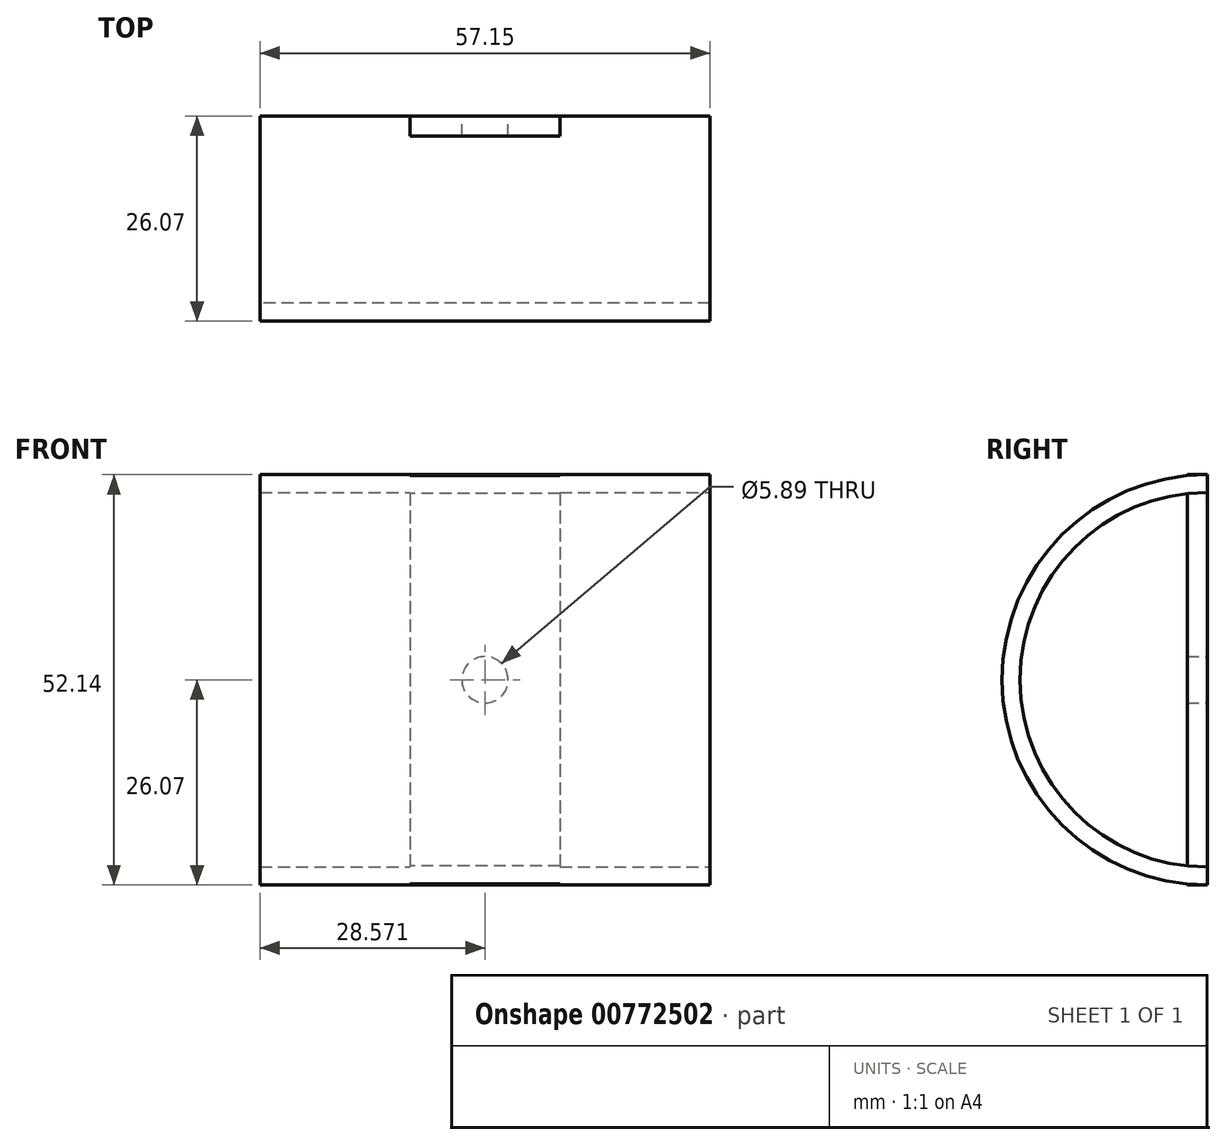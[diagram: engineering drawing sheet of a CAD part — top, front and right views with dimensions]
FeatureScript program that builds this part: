
annotation { "Feature Type Name" : "Feature", "Feature Type Description" : "" }
export const myFeature = defineFeature(function(context is Context, id is Id, definition is map)
    precondition{}
    {
        {
            var Q0;
            Q0=qCreatedBy(makeId("Front.planeOp"),FACE);
            var sketch = newSketch(context, id + "F0", { "sketchPlane" : qUnion([Q0])});
            skLineSegment(sketch, "E0.bottom", {"start": v(-15.82, 23.8) * mm, "end": v(41.33, 23.8) * mm});
            skLineSegment(sketch, "E0.top", {"start": v(-15.82, 26.07) * mm, "end": v(41.33, 26.07) * mm});
            skLineSegment(sketch, "E0.left", {"start": v(-15.82, 23.8) * mm, "end": v(-15.82, 26.07) * mm});
            skLineSegment(sketch, "E0.right", {"start": v(41.33, 23.8) * mm, "end": v(41.33, 26.07) * mm});
            skLineSegment(sketch, "E1", {"start": v(-10.59, 0) * mm, "end": v(36.32, 0) * mm});
            skSolve(sketch);
        }
        {
            var Q0;
            Q0=makeQuery(id+"F0.imprint","IMPRINT",FACE,{"disambiguationData":[TD([[makeQuery(id+"F0.imprint","IMPRINT",EDGE,{"derivedFrom":sQuery(id+"F0.wireOp",EDGE,"E0.bottom")}),1.0]])]});
            var Q1;
            Q1=sQuery(id+"F0.wireOp",EDGE,"E1");
            revolve(context, id + "F1", {"surfaceOperationType" : NewSurfaceOperationType.NEW, "entities" : qUnion([Q0]), "axis" : qUnion([Q1]), "revolveType" : RevolveType.ONE_DIRECTION, "angle" : 180 * degree});
        }
        {
            var Q0;
            Q0=qCreatedBy(makeId("Front.planeOp"),FACE);
            var sketch = newSketch(context, id + "F2", { "sketchPlane" : qUnion([Q0])});
            skCircle(sketch, "E2", {"center": v(12.75, 0) * mm, "radius": 2.94 * mm});
            skLineSegment(sketch, "E3.0", {"start": v(-15.82, 26.07) * mm, "end": v(41.33, 26.07) * mm});
            skLineSegment(sketch, "E4.0", {"start": v(-15.82, -26.07) * mm, "end": v(41.33, -26.07) * mm});
            skLineSegment(sketch, "E5.bottom", {"start": v(22.28, 26.07) * mm, "end": v(3.23, 26.07) * mm});
            skLineSegment(sketch, "E5.top", {"start": v(22.28, -26.07) * mm, "end": v(3.23, -26.07) * mm});
            skLineSegment(sketch, "E5.left", {"start": v(22.28, 26.07) * mm, "end": v(22.28, -26.07) * mm});
            skLineSegment(sketch, "E5.right", {"start": v(3.23, 26.07) * mm, "end": v(3.23, -26.07) * mm});
            skSolve(sketch);
        }
        {
            var Q0;
            Q0=makeQuery(id+"F2.imprint","IMPRINT",FACE,{"disambiguationData":[TD([[makeQuery(id+"F2.imprint","IMPRINT",EDGE,{"derivedFrom":sQuery(id+"F2.wireOp",EDGE,"E2")}),-1.0]])]});
            extrude(context, id + "F3", {"entities" : qUnion([Q0]), "operationType" : NewBodyOperationType.ADD, "depth" : 2.54 * mm, "offsetDistance" : 25.4 * mm});
        }
    });
